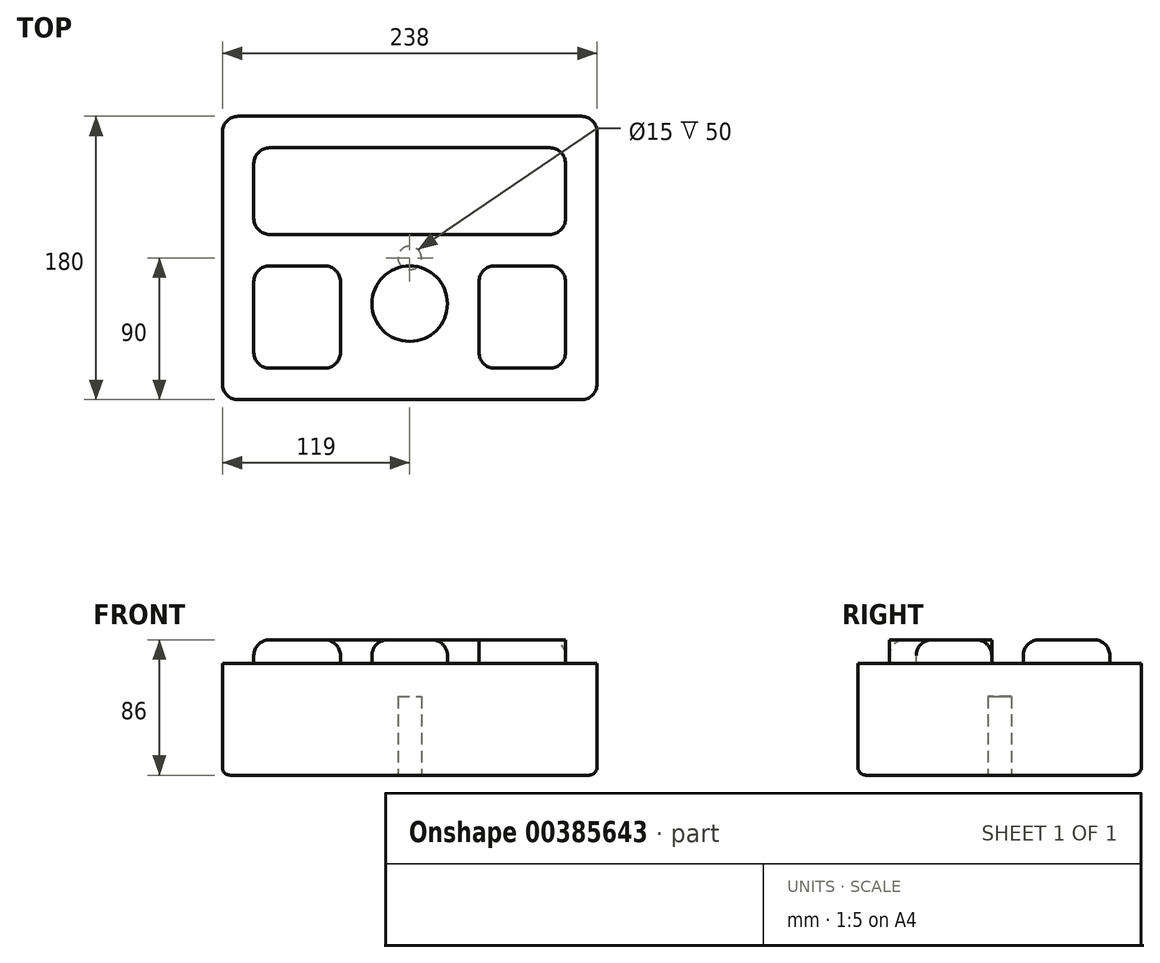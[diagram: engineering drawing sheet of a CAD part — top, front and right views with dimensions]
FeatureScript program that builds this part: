
annotation { "Feature Type Name" : "Feature", "Feature Type Description" : "" }
export const myFeature = defineFeature(function(context is Context, id is Id, definition is map)
    precondition{}
    {
        {
            var Q0;
            Q0=qCreatedBy(makeId("Top.planeOp"),FACE);
            var sketch = newSketch(context, id + "F0", { "sketchPlane" : qUnion([Q0])});
            skLineSegment(sketch, "E0.bottom", {"start": v(-119, 90) * mm, "end": v(119, 90) * mm});
            skLineSegment(sketch, "E0.top", {"start": v(-119, -90) * mm, "end": v(119, -90) * mm});
            skLineSegment(sketch, "E0.left", {"start": v(-119, 90) * mm, "end": v(-119, -90) * mm});
            skLineSegment(sketch, "E0.right", {"start": v(119, 90) * mm, "end": v(119, -90) * mm});
            skSolve(sketch);
        }
        {
            var Q0;
            Q0 = qSketchRegion(id + "F0", true);
            extrude(context, id + "F1", {"entities" : qUnion([Q0]), "depth" : 86 * mm});
        }
        {
            var Q0;
            Q0=makeQuery(id+"F1.opExtrude","CAP_FACE",FACE,{"disambiguationData":[OSD([sQuery(id+"F0.wireOp",EDGE,"E0.bottom"),sQuery(id+"F0.wireOp",EDGE,"E0.top"),sQuery(id+"F0.wireOp",EDGE,"E0.left"),sQuery(id+"F0.wireOp",EDGE,"E0.right")])],"isStart":false});
            var sketch = newSketch(context, id + "F2", { "sketchPlane" : qUnion([Q0])});
            skLineSegment(sketch, "E1.bottom", {"start": v(-99, 70) * mm, "end": v(99, 70) * mm});
            skLineSegment(sketch, "E1.top", {"start": v(-99, 15) * mm, "end": v(99, 15) * mm});
            skLineSegment(sketch, "E1.left", {"start": v(-99, 70) * mm, "end": v(-99, 15) * mm});
            skLineSegment(sketch, "E1.right", {"start": v(99, 70) * mm, "end": v(99, 15) * mm});
            skLineSegment(sketch, "E2.bottom", {"start": v(-99, -5) * mm, "end": v(-44, -5) * mm});
            skLineSegment(sketch, "E2.top", {"start": v(-99, -70) * mm, "end": v(-44, -70) * mm});
            skLineSegment(sketch, "E2.left", {"start": v(-99, -5) * mm, "end": v(-99, -70) * mm});
            skLineSegment(sketch, "E2.right", {"start": v(-44, -5) * mm, "end": v(-44, -70) * mm});
            skLineSegment(sketch, "E3.bottom", {"start": v(99, -5) * mm, "end": v(44, -5) * mm});
            skLineSegment(sketch, "E3.top", {"start": v(99, -70) * mm, "end": v(44, -70) * mm});
            skLineSegment(sketch, "E3.left", {"start": v(99, -5) * mm, "end": v(99, -70) * mm});
            skLineSegment(sketch, "E3.right", {"start": v(44, -5) * mm, "end": v(44, -70) * mm});
            skLineSegment(sketch, "E4.bottom", {"start": v(24, -5) * mm, "end": v(-24, -5) * mm, "construction": true});
            skLineSegment(sketch, "E4.top", {"start": v(24, -70) * mm, "end": v(-24, -70) * mm, "construction": true});
            skLineSegment(sketch, "E4.left", {"start": v(24, -5) * mm, "end": v(24, -70) * mm, "construction": true});
            skLineSegment(sketch, "E4.right", {"start": v(-24, -5) * mm, "end": v(-24, -70) * mm, "construction": true});
            skCircle(sketch, "E5", {"center": v(0, -29) * mm, "radius": 24 * mm});
            skSolve(sketch);
        }
        {
            var Q0;
            Q0=makeQuery(id+"F2.imprint","IMPRINT",FACE,{"disambiguationData":[TD([[makeQuery(id+"F2.imprint","IMPRINT",EDGE,{"derivedFrom":sQuery(id+"F2.wireOp",EDGE,"E1.bottom")}),1.0]])]});
            extrude(context, id + "F3", {"entities" : qUnion([Q0]), "operationType" : NewBodyOperationType.REMOVE, "oppositeDirection" : true, "depth" : 15 * mm});
        }
        {
            var Q0;
            Q0=makeQuery(id+"F1.opExtrude","SWEPT_EDGE",EDGE,{"disambiguationData":[OSD([sQuery(id+"F0.wireOp",EDGE,"E0.top"),sQuery(id+"F0.wireOp",EDGE,"E0.left")])]});
            var Q1;
            Q1=makeQuery(id+"F1.opExtrude","SWEPT_EDGE",EDGE,{"disambiguationData":[OSD([sQuery(id+"F0.wireOp",EDGE,"E0.top"),sQuery(id+"F0.wireOp",EDGE,"E0.right")])]});
            var Q2;
            Q2=makeQuery(id+"F1.opExtrude","SWEPT_EDGE",EDGE,{"disambiguationData":[OSD([sQuery(id+"F0.wireOp",EDGE,"E0.bottom"),sQuery(id+"F0.wireOp",EDGE,"E0.left")])]});
            var Q3;
            Q3=makeQuery(id+"F1.opExtrude","SWEPT_EDGE",EDGE,{"disambiguationData":[OSD([sQuery(id+"F0.wireOp",EDGE,"E0.bottom"),sQuery(id+"F0.wireOp",EDGE,"E0.right")])]});
            var Q4;
            Q4=makeQuery(id+"F3.boolean.opBoolean","COPY",EDGE,{"derivedFrom":makeQuery(id+"F3.opExtrude","SWEPT_EDGE",EDGE,{"disambiguationData":[OSD([sQuery(id+"F2.wireOp",EDGE,"E1.bottom"),sQuery(id+"F2.wireOp",EDGE,"E1.left")])]})});
            var Q5;
            Q5=makeQuery(id+"F3.boolean.opBoolean","COPY",EDGE,{"derivedFrom":makeQuery(id+"F3.opExtrude","SWEPT_EDGE",EDGE,{"disambiguationData":[OSD([sQuery(id+"F2.wireOp",EDGE,"E2.bottom"),sQuery(id+"F2.wireOp",EDGE,"E2.left")])]})});
            var Q6;
            Q6=makeQuery(id+"F3.boolean.opBoolean","COPY",EDGE,{"derivedFrom":makeQuery(id+"F3.opExtrude","SWEPT_EDGE",EDGE,{"disambiguationData":[OSD([sQuery(id+"F2.wireOp",EDGE,"E2.top"),sQuery(id+"F2.wireOp",EDGE,"E2.left")])]})});
            var Q7;
            Q7=makeQuery(id+"F3.boolean.opBoolean","COPY",EDGE,{"derivedFrom":makeQuery(id+"F3.opExtrude","SWEPT_EDGE",EDGE,{"disambiguationData":[OSD([sQuery(id+"F2.wireOp",EDGE,"E2.bottom"),sQuery(id+"F2.wireOp",EDGE,"E2.right")])]})});
            var Q8;
            Q8=makeQuery(id+"F3.boolean.opBoolean","COPY",EDGE,{"derivedFrom":makeQuery(id+"F3.opExtrude","SWEPT_EDGE",EDGE,{"disambiguationData":[OSD([sQuery(id+"F2.wireOp",EDGE,"E1.bottom"),sQuery(id+"F2.wireOp",EDGE,"E1.right")])]})});
            var Q9;
            Q9=makeQuery(id+"F3.boolean.opBoolean","COPY",EDGE,{"derivedFrom":makeQuery(id+"F3.opExtrude","SWEPT_EDGE",EDGE,{"disambiguationData":[OSD([sQuery(id+"F2.wireOp",EDGE,"E3.bottom"),sQuery(id+"F2.wireOp",EDGE,"E3.left")])]})});
            var Q10;
            Q10=makeQuery(id+"F3.boolean.opBoolean","COPY",EDGE,{"derivedFrom":makeQuery(id+"F3.opExtrude","SWEPT_EDGE",EDGE,{"disambiguationData":[OSD([sQuery(id+"F2.wireOp",EDGE,"E3.bottom"),sQuery(id+"F2.wireOp",EDGE,"E3.right")])]})});
            var Q11;
            Q11=makeQuery(id+"F3.boolean.opBoolean","COPY",EDGE,{"derivedFrom":makeQuery(id+"F3.opExtrude","SWEPT_EDGE",EDGE,{"disambiguationData":[OSD([sQuery(id+"F2.wireOp",EDGE,"E3.top"),sQuery(id+"F2.wireOp",EDGE,"E3.right")])]})});
            var Q12;
            Q12=makeQuery(id+"F3.boolean.opBoolean","COPY",EDGE,{"derivedFrom":makeQuery(id+"F3.opExtrude","SWEPT_EDGE",EDGE,{"disambiguationData":[OSD([sQuery(id+"F2.wireOp",EDGE,"E1.top"),sQuery(id+"F2.wireOp",EDGE,"E1.left")])]})});
            var Q13;
            Q13=makeQuery(id+"F3.boolean.opBoolean","COPY",EDGE,{"derivedFrom":makeQuery(id+"F3.opExtrude","SWEPT_EDGE",EDGE,{"disambiguationData":[OSD([sQuery(id+"F2.wireOp",EDGE,"E2.top"),sQuery(id+"F2.wireOp",EDGE,"E2.right")])]})});
            var Q14;
            Q14=makeQuery(id+"F3.boolean.opBoolean","COPY",EDGE,{"derivedFrom":makeQuery(id+"F3.opExtrude","SWEPT_EDGE",EDGE,{"disambiguationData":[OSD([sQuery(id+"F2.wireOp",EDGE,"E3.top"),sQuery(id+"F2.wireOp",EDGE,"E3.left")])]})});
            var Q15;
            Q15=makeQuery(id+"F3.boolean.opBoolean","COPY",EDGE,{"derivedFrom":makeQuery(id+"F3.opExtrude","SWEPT_EDGE",EDGE,{"disambiguationData":[OSD([sQuery(id+"F2.wireOp",EDGE,"E1.top"),sQuery(id+"F2.wireOp",EDGE,"E1.right")])]})});
            fillet(context, id + "F4", {"entities" : qUnion([Q0, Q1, Q2, Q3, Q4, Q5, Q6, Q7, Q8, Q9, Q10, Q11, Q12, Q13, Q14, Q15]), "radius" : 10 * mm, "tangentPropagation" : true, "allowEdgeOverflow" : false});
        }
        {
            var Q0;
            Q0=makeQuery(id+"F3.boolean.opBoolean","COPY",EDGE,{"derivedFrom":makeQuery(id+"F3.opExtrude","CAP_EDGE",EDGE,{"disambiguationData":[OSD([sQuery(id+"F2.wireOp",EDGE,"E1.top")])],"isStart":true})});
            var Q1;
            Q1=makeQuery(id+"F3.boolean.opBoolean","COPY",EDGE,{"derivedFrom":makeQuery(id+"F3.opExtrude","CAP_EDGE",EDGE,{"disambiguationData":[OSD([sQuery(id+"F2.wireOp",EDGE,"E2.bottom")])],"isStart":true})});
            var Q2;
            Q2=makeQuery(id+"F3.boolean.opBoolean","COPY",EDGE,{"derivedFrom":makeQuery(id+"F3.opExtrude","CAP_EDGE",EDGE,{"disambiguationData":[OSD([sQuery(id+"F2.wireOp",EDGE,"E5")])],"isStart":true})});
            var Q3;
            Q3=makeQuery(id+"F3.boolean.opBoolean","COPY",EDGE,{"derivedFrom":makeQuery(id+"F3.opExtrude","CAP_EDGE",EDGE,{"disambiguationData":[OSD([sQuery(id+"F2.wireOp",EDGE,"E3.bottom")])],"isStart":true})});
            fillet(context, id + "F5", {"entities" : qUnion([Q0, Q1, Q2, Q3]), "radius" : 10 * mm, "tangentPropagation" : true, "allowEdgeOverflow" : false});
        }
        {
            var Q0;
            Q0=makeQuery(id+"F3.boolean.opBoolean","COPY",EDGE,{"derivedFrom":makeQuery(id+"F3.opExtrude","CAP_EDGE",EDGE,{"disambiguationData":[OSD([sQuery(id+"F0.wireOp",EDGE,"E0.left")])],"isStart":false})});
            var Q1;
            Q1=makeQuery(id+"F1.opExtrude","CAP_EDGE",EDGE,{"disambiguationData":[OSD([sQuery(id+"F0.wireOp",EDGE,"E0.left")])],"isStart":true});
            fillet(context, id + "F6", {"entities" : qUnion([Q0, Q1]), "radius" : 5 * mm, "tangentPropagation" : true, "allowEdgeOverflow" : false});
        }
        {
            var Q0;
            Q0=makeQuery(id+"F1.opExtrude","CAP_FACE",FACE,{"disambiguationData":[OSD([sQuery(id+"F0.wireOp",EDGE,"E0.bottom"),sQuery(id+"F0.wireOp",EDGE,"E0.top"),sQuery(id+"F0.wireOp",EDGE,"E0.left"),sQuery(id+"F0.wireOp",EDGE,"E0.right")])],"isStart":true});
            var sketch = newSketch(context, id + "F7", { "sketchPlane" : qUnion([Q0])});
            skCircle(sketch, "E6", {"center": v(0, 0) * mm, "radius": 7.5 * mm});
            skSolve(sketch);
        }
        {
            var Q0;
            Q0 = qSketchRegion(id + "F7", true);
            extrude(context, id + "F8", {"entities" : qUnion([Q0]), "operationType" : NewBodyOperationType.REMOVE, "oppositeDirection" : true, "depth" : 50 * mm});
        }
    });
